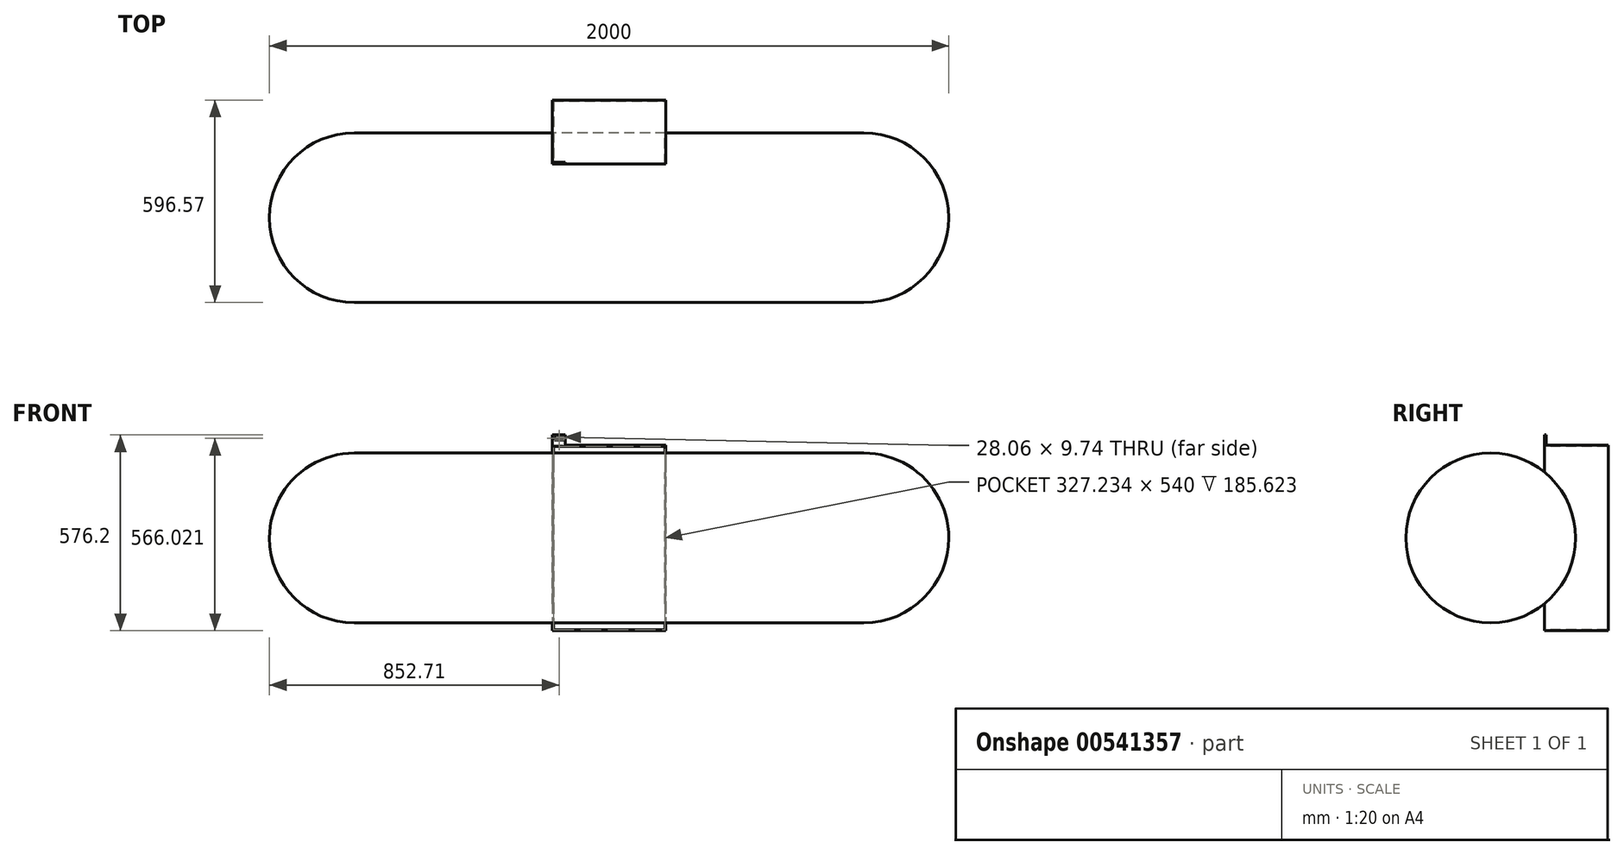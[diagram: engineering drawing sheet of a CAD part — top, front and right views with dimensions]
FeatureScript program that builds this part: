
annotation { "Feature Type Name" : "Feature", "Feature Type Description" : "" }
export const myFeature = defineFeature(function(context is Context, id is Id, definition is map)
    precondition{}
    {
        {
            var Q0;
            Q0=qCreatedBy(makeId("Front.planeOp"),FACE);
            var sketch = newSketch(context, id + "F0", { "sketchPlane" : qUnion([Q0])});
            skLineSegment(sketch, "E0", {"start": v(-1000, 0) * mm, "end": v(1000, 0) * mm});
            skArc(sketch, "E1", {"start": v(1000, 0) * mm, "mid": v(926.78, 176.78) * mm, "end": v(750, 250) * mm});
            skArc(sketch, "E2", {"start": v(-750, 250) * mm, "mid": v(-926.78, 176.78) * mm, "end": v(-1000, 0) * mm});
            skLineSegment(sketch, "E3", {"start": v(-750, 250) * mm, "end": v(750, 250) * mm});
            skSolve(sketch);
        }
        {
            var Q0;
            Q0 = qSketchRegion(id + "F0", true);
            var Q1;
            Q1=sQuery(id+"F0.wireOp",EDGE,"E0");
            revolve(context, id + "F1", {"entities" : qUnion([Q0]), "axis" : qUnion([Q1]), "revolveType" : RevolveType.FULL});
        }
        {
            var Q0;
            Q0=qCreatedBy(makeId("Top.planeOp"),FACE);
            var sketch = newSketch(context, id + "F2", { "sketchPlane" : qUnion([Q0])});
            skLineSegment(sketch, "E4.bottom", {"start": v(-166.62, 346.57) * mm, "end": v(166.62, 346.57) * mm});
            skLineSegment(sketch, "E4.top", {"start": v(-166.62, 157.95) * mm, "end": v(166.62, 157.95) * mm});
            skLineSegment(sketch, "E4.left", {"start": v(-166.62, 346.57) * mm, "end": v(-166.62, 157.95) * mm});
            skLineSegment(sketch, "E4.right", {"start": v(166.62, 346.57) * mm, "end": v(166.62, 157.95) * mm});
            skLineSegment(sketch, "E5", {"start": v(0, 157.95) * mm, "end": v(0, 0) * mm, "construction": true});
            skSolve(sketch);
        }
        {
            var Q0;
            Q0=makeQuery(id+"F2.imprint","IMPRINT",FACE,{"disambiguationData":[TD([[makeQuery(id+"F2.imprint","IMPRINT",EDGE,{"derivedFrom":sQuery(id+"F2.wireOp",EDGE,"E4.bottom")}),-1.0]])]});
            extrude(context, id + "F3", {"entities" : qUnion([Q0]), "endBound" : BoundingType.SYMMETRIC, "depth" : 546 * mm, "offsetDistance" : 25 * mm});
        }
        {
            var Q0;
            Q0=makeQuery(id+"F3.opExtrude","SWEPT_BODY",BODY,{"disambiguationData":[OSD([sQuery(id+"F2.wireOp",EDGE,"E4.bottom"),sQuery(id+"F2.wireOp",EDGE,"E4.top"),sQuery(id+"F2.wireOp",EDGE,"E4.left"),sQuery(id+"F2.wireOp",EDGE,"E4.right")])]});
            var Q1;
            Q1=makeQuery(id+"F1.opRevolve","SWEPT_BODY",BODY,{"disambiguationData":[OSD([sQuery(id+"F0.wireOp",EDGE,"E0"),sQuery(id+"F0.wireOp",EDGE,"E1"),sQuery(id+"F0.wireOp",EDGE,"E2"),sQuery(id+"F0.wireOp",EDGE,"E3")])]});
            booleanBodies(context, id + "F4", {"operationType" : BooleanOperationType.INTERSECTION, "tools" : qUnion([Q0, Q1]), "keepTools" : true});
        }
        {
            var Q0;
            Q0=makeQuery(id+"F4.opBoolean","INTERSECT",BODY,{"derivedFrom":[makeQuery(id+"F1.opRevolve","SWEPT_BODY",BODY,{"disambiguationData":[OSD([sQuery(id+"F0.wireOp",EDGE,"E0"),sQuery(id+"F0.wireOp",EDGE,"E1"),sQuery(id+"F0.wireOp",EDGE,"E2"),sQuery(id+"F0.wireOp",EDGE,"E3")])]}),makeQuery(id+"F3.opExtrude","SWEPT_BODY",BODY,{"disambiguationData":[OSD([sQuery(id+"F2.wireOp",EDGE,"E4.bottom"),sQuery(id+"F2.wireOp",EDGE,"E4.top"),sQuery(id+"F2.wireOp",EDGE,"E4.left"),sQuery(id+"F2.wireOp",EDGE,"E4.right")])]})]});
            var Q1;
            Q1=makeQuery(id+"F3.opExtrude","SWEPT_BODY",BODY,{"disambiguationData":[OSD([sQuery(id+"F2.wireOp",EDGE,"E4.bottom"),sQuery(id+"F2.wireOp",EDGE,"E4.top"),sQuery(id+"F2.wireOp",EDGE,"E4.left"),sQuery(id+"F2.wireOp",EDGE,"E4.right")])]});
            booleanBodies(context, id + "F5", {"operationType" : BooleanOperationType.SUBTRACTION, "tools" : qUnion([Q0]), "targets" : qUnion([Q1])});
        }
        {
            var Q0;
            Q0=makeQuery(id+"F5.opBoolean","COPY",FACE,{"derivedFrom":makeQuery(id+"F4.opBoolean","COPY",FACE,{"derivedFrom":makeQuery(id+"F1.opRevolve","SWEPT_FACE",FACE,{"disambiguationData":[OSD([sQuery(id+"F0.wireOp",EDGE,"E3")])]})})});
            var Q1;
            {var subQ0=sQuery(id+"F2.wireOp",EDGE,"E4.right");var subQ1=sQuery(id+"F2.wireOp",EDGE,"E4.left");var subQ2=sQuery(id+"F2.wireOp",EDGE,"E4.top");Q1=makeQuery(id+"F5.opBoolean","SPLIT",FACE,{"disambiguationData":[TD([makeQuery(id+"F3.opExtrude","CAP_FACE",FACE,{"disambiguationData":[OSD([sQuery(id+"F2.wireOp",EDGE,"E4.bottom"),subQ2,subQ1,subQ0])],"isStart":false})])],"derivedFrom":makeQuery(id+"F3.opExtrude","SWEPT_FACE",FACE,{"disambiguationData":[OSD([subQ2])]})});}
            var Q2;
            {var subQ0=sQuery(id+"F2.wireOp",EDGE,"E4.right");var subQ1=sQuery(id+"F2.wireOp",EDGE,"E4.left");var subQ2=sQuery(id+"F2.wireOp",EDGE,"E4.top");Q2=makeQuery(id+"F5.opBoolean","SPLIT",FACE,{"disambiguationData":[TD([makeQuery(id+"F3.opExtrude","CAP_FACE",FACE,{"disambiguationData":[OSD([sQuery(id+"F2.wireOp",EDGE,"E4.bottom"),subQ2,subQ1,subQ0])],"isStart":true})])],"derivedFrom":makeQuery(id+"F3.opExtrude","SWEPT_FACE",FACE,{"disambiguationData":[OSD([subQ2])]})});}
            shell(context, id + "F6", {"entities" : qUnion([Q0, Q1, Q2]), "thickness" : 3 * mm});
        }
        {
            var Q0;
            Q0=makeQuery(id+"F3.opExtrude","CAP_FACE",FACE,{"disambiguationData":[OSD([sQuery(id+"F2.wireOp",EDGE,"E4.bottom"),sQuery(id+"F2.wireOp",EDGE,"E4.top"),sQuery(id+"F2.wireOp",EDGE,"E4.left"),sQuery(id+"F2.wireOp",EDGE,"E4.right")])],"isStart":false});
            var sketch = newSketch(context, id + "F7", { "sketchPlane" : qUnion([Q0])});
            skLineSegment(sketch, "E6.bottom", {"start": v(-166.62, 157.95) * mm, "end": v(-129.26, 157.95) * mm});
            skLineSegment(sketch, "E6.top", {"start": v(-166.62, 163.11) * mm, "end": v(-129.26, 163.11) * mm});
            skLineSegment(sketch, "E6.left", {"start": v(-166.62, 157.95) * mm, "end": v(-166.62, 163.11) * mm});
            skLineSegment(sketch, "E6.right", {"start": v(-129.26, 157.95) * mm, "end": v(-129.26, 163.11) * mm});
            skSolve(sketch);
        }
        {
            var Q0;
            Q0 = qSketchRegion(id + "F7", true);
            extrude(context, id + "F8", {"entities" : qUnion([Q0]), "operationType" : NewBodyOperationType.ADD, "depth" : 30.2 * mm, "offsetDistance" : 25 * mm});
        }
        {
            var Q0;
            {var subQ0=sQuery(id+"F2.wireOp",EDGE,"E4.right");var subQ1=sQuery(id+"F2.wireOp",EDGE,"E4.left");var subQ2=sQuery(id+"F2.wireOp",EDGE,"E4.top");Q0=makeQuery(id+"F8.boolean.opBoolean","MERGE",FACE,{"derivedFrom":[makeQuery(id+"F5.opBoolean","SPLIT",FACE,{"disambiguationData":[TD([makeQuery(id+"F3.opExtrude","CAP_FACE",FACE,{"disambiguationData":[OSD([sQuery(id+"F2.wireOp",EDGE,"E4.bottom"),subQ2,subQ1,subQ0])],"isStart":false})])],"derivedFrom":makeQuery(id+"F3.opExtrude","SWEPT_FACE",FACE,{"disambiguationData":[OSD([subQ2])]})}),makeQuery(id+"F8.opExtrude","SWEPT_FACE",FACE,{"disambiguationData":[OSD([sQuery(id+"F7.wireOp",EDGE,"E6.bottom")])]})]});}
            var sketch = newSketch(context, id + "F9", { "sketchPlane" : qUnion([Q0])});
            skLineSegment(sketch, "E7.bottom", {"start": v(-161.32, 297.89) * mm, "end": v(-133.26, 297.89) * mm});
            skLineSegment(sketch, "E7.top", {"start": v(-161.32, 288.15) * mm, "end": v(-133.26, 288.15) * mm});
            skLineSegment(sketch, "E7.left", {"start": v(-161.32, 297.89) * mm, "end": v(-161.32, 288.15) * mm});
            skLineSegment(sketch, "E7.right", {"start": v(-133.26, 297.89) * mm, "end": v(-133.26, 288.15) * mm});
            skSolve(sketch);
        }
        {
            var Q0;
            Q0=makeQuery(id+"F9.imprint","IMPRINT",FACE,{"disambiguationData":[TD([[makeQuery(id+"F9.imprint","IMPRINT",EDGE,{"derivedFrom":sQuery(id+"F9.wireOp",EDGE,"E7.bottom")}),-1.0]])]});
            extrude(context, id + "F10", {"entities" : qUnion([Q0]), "operationType" : NewBodyOperationType.REMOVE, "oppositeDirection" : true, "depth" : 25 * mm, "offsetDistance" : 25 * mm});
        }
    });
